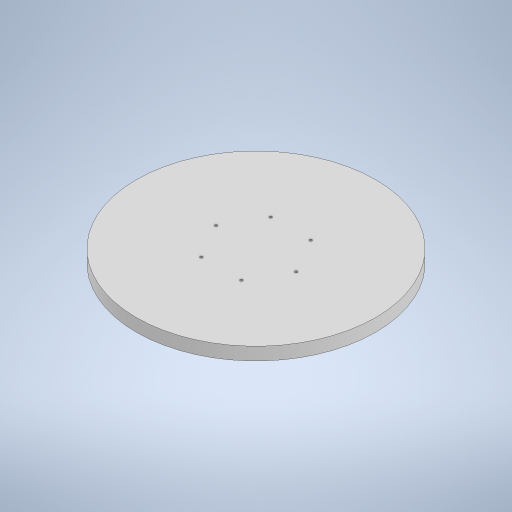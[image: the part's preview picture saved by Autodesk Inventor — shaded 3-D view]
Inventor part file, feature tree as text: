
AUTODESK INVENTOR PART (.ipt)
format: ipt  version: 2023 (Build 270158000, 158)  size: 292,352 bytes
history: native  units: in
note: dims shown in document units (in); Inventor stores cm internally (conversion verified against a paired STEP export)
features: extrude x2, sketch x1
ambient origin geometry x8: Origin, YZ Plane, XZ Plane, XY Plane, X Axis, Y Axis, Z Axis, Center Point
bodies: Solid1 (feature_tree)
feature tree (3):
  sketch  "Sketch1"  dims[d0=20.0in d1=1.0in d2=45.0deg d3=0.0in d4=0.0in d5=45.0deg d6=0.5in d7=0.5in d8=0.5in d9=0.5in d10=12.0in d11=8.0in d12=7.0in d13=0.5in d14=0.25in d15=5.75in d16=2.3622in d18=360.0deg d20=0.25in d21=3.75in d22=2.3622in d24=360.0deg d26=0.2in d27=0.2in d28=0.0in d29=1.0in d30=0.0in]
  extrude  "Extrusion1"  Depth=1.0in
  extrude  "Extrusion2"  TaperAngle=45.0deg  [1 undecoded]
note: 1 required parameter value undecoded (feature->parameter linkage not recoverable at this tier; creation-order binding heuristic only, values carry confidence <= 0.55)
